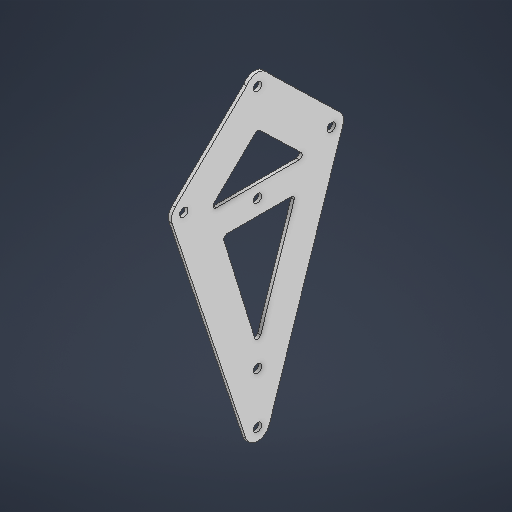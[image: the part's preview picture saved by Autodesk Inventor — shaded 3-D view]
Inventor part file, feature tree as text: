
AUTODESK INVENTOR PART (.ipt)
format: ipt  version: 2025.2 (Build 292293000, 293)  size: 229,376 bytes
history: native  units: in
note: dims shown in document units (in); Inventor stores cm internally (conversion verified against a paired STEP export)
features: extrude x1, sketch x1
ambient origin geometry x8: Origin, YZ Plane, XZ Plane, XY Plane, X Axis, Y Axis, Z Axis, Center Point
bodies: Solid1 (feature_tree)
feature tree (2):
  extrude  "Extrusion1"  Depth=0.0625in
  sketch  "Sketch1"  dims[d0=0.5in d1=0.5in d2=0.5in d3=0.172in d4=0.172in d5=1.0in d6=1.0in d7=0.172in d8=0.172in d9=0.172in d10=0.172in d11=0.0625in d12=0.0625in d13=0.0in]
